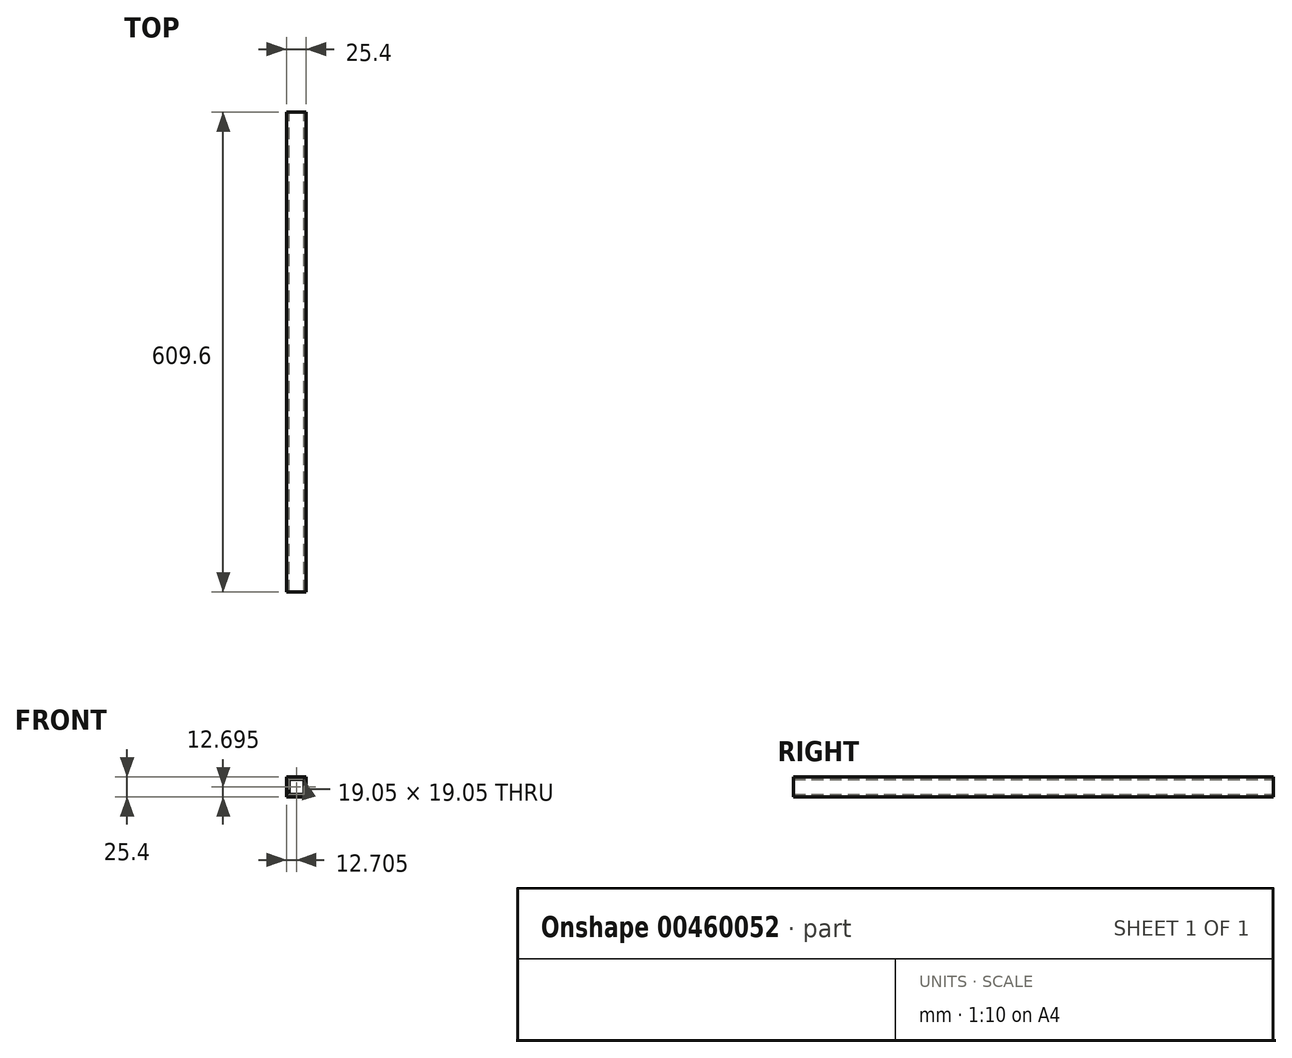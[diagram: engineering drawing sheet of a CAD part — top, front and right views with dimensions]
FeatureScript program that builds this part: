
annotation { "Feature Type Name" : "Feature", "Feature Type Description" : "" }
export const myFeature = defineFeature(function(context is Context, id is Id, definition is map)
    precondition{}
    {
        {
            var Q0;
            Q0=qCreatedBy(makeId("Front.planeOp"),FACE);
            var sketch = newSketch(context, id + "F0", { "sketchPlane" : qUnion([Q0])});
            skLineSegment(sketch, "E0.bottom", {"start": v(-22.23, 22.23) * mm, "end": v(3.17, 22.23) * mm});
            skLineSegment(sketch, "E0.top", {"start": v(-22.23, -3.18) * mm, "end": v(3.18, -3.18) * mm});
            skLineSegment(sketch, "E0.left", {"start": v(-22.23, 22.23) * mm, "end": v(-22.23, -3.18) * mm});
            skLineSegment(sketch, "E0.right", {"start": v(3.17, 22.23) * mm, "end": v(3.18, -3.18) * mm});
            skLineSegment(sketch, "E1.bottom", {"start": v(-19.05, 19.05) * mm, "end": v(0, 19.05) * mm});
            skLineSegment(sketch, "E1.top", {"start": v(-19.05, 0) * mm, "end": v(0, 0) * mm});
            skLineSegment(sketch, "E1.left", {"start": v(-19.05, 19.05) * mm, "end": v(-19.05, 0) * mm});
            skLineSegment(sketch, "E1.right", {"start": v(0, 19.05) * mm, "end": v(0, 0) * mm});
            skSolve(sketch);
        }
        {
            var Q0;
            Q0=qSketchRegion(id+"F0",true);
            extrude(context, id + "F1", {"entities" : qUnion([Q0]), "depth" : 609.6 * mm});
        }
    });
